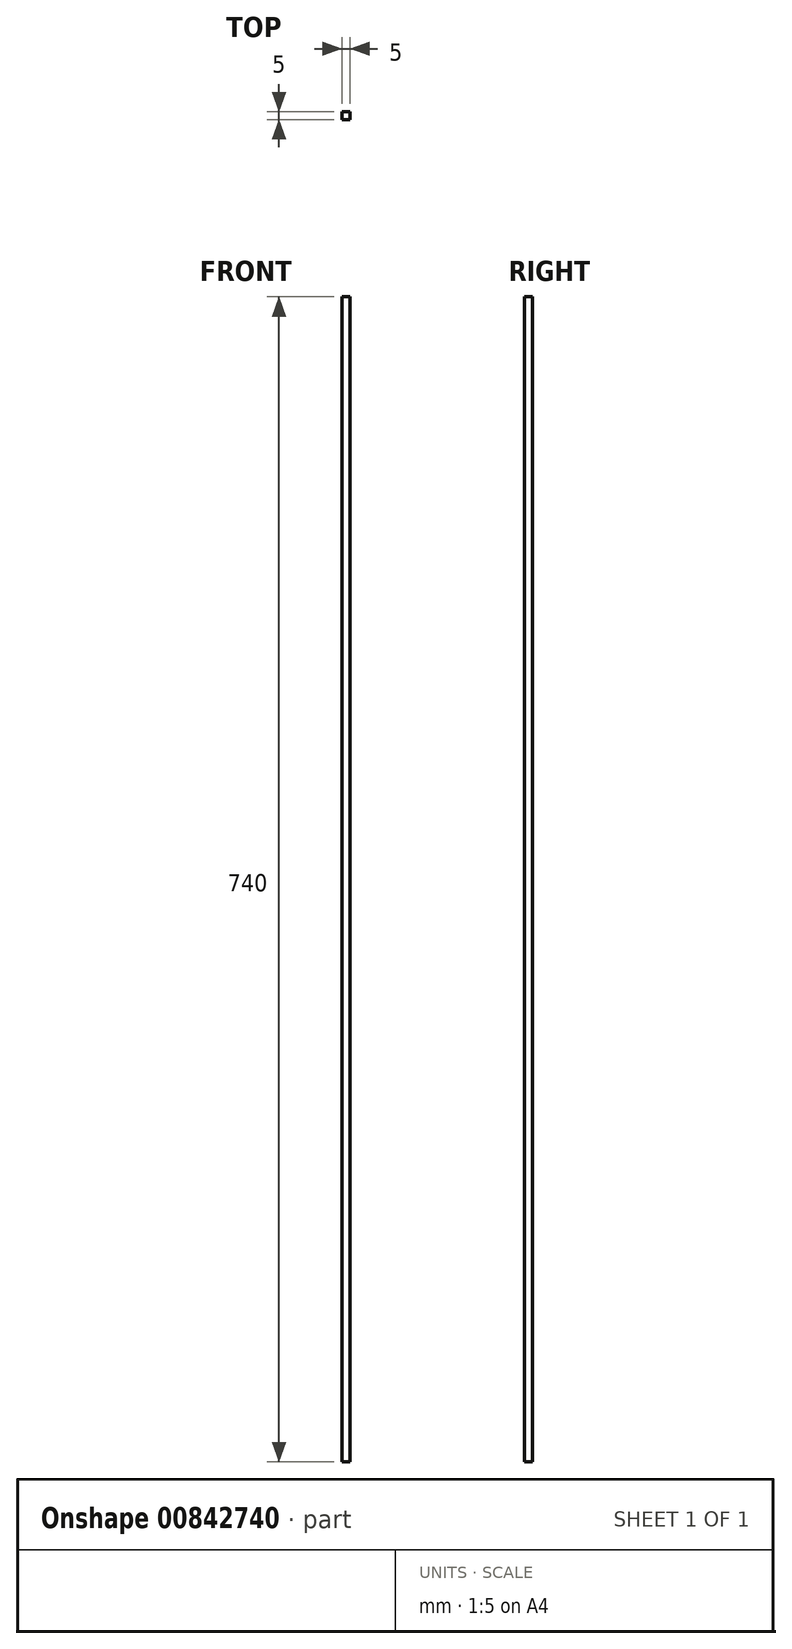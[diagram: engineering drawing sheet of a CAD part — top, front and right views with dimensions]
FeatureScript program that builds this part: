
annotation { "Feature Type Name" : "Feature", "Feature Type Description" : "" }
export const myFeature = defineFeature(function(context is Context, id is Id, definition is map)
    precondition{}
    {
        {
            var Q0;
            Q0=qCreatedBy(makeId("Top.planeOp"),FACE);
            var sketch = newSketch(context, id + "F0", { "sketchPlane" : qUnion([Q0])});
            skLineSegment(sketch, "E0.bottom", {"start": v(0, 0) * mm, "end": v(5, 0) * mm});
            skLineSegment(sketch, "E0.top", {"start": v(0, 5) * mm, "end": v(5, 5) * mm});
            skLineSegment(sketch, "E0.left", {"start": v(0, 0) * mm, "end": v(0, 5) * mm});
            skLineSegment(sketch, "E0.right", {"start": v(5, 0) * mm, "end": v(5, 5) * mm});
            skSolve(sketch);
        }
        {
            var Q0;
            Q0=qSketchRegion(id+"F0",true);
            extrude(context, id + "F1", {"entities" : qUnion([Q0]), "depth" : 740 * mm, "offsetDistance" : 25 * mm});
        }
    });
